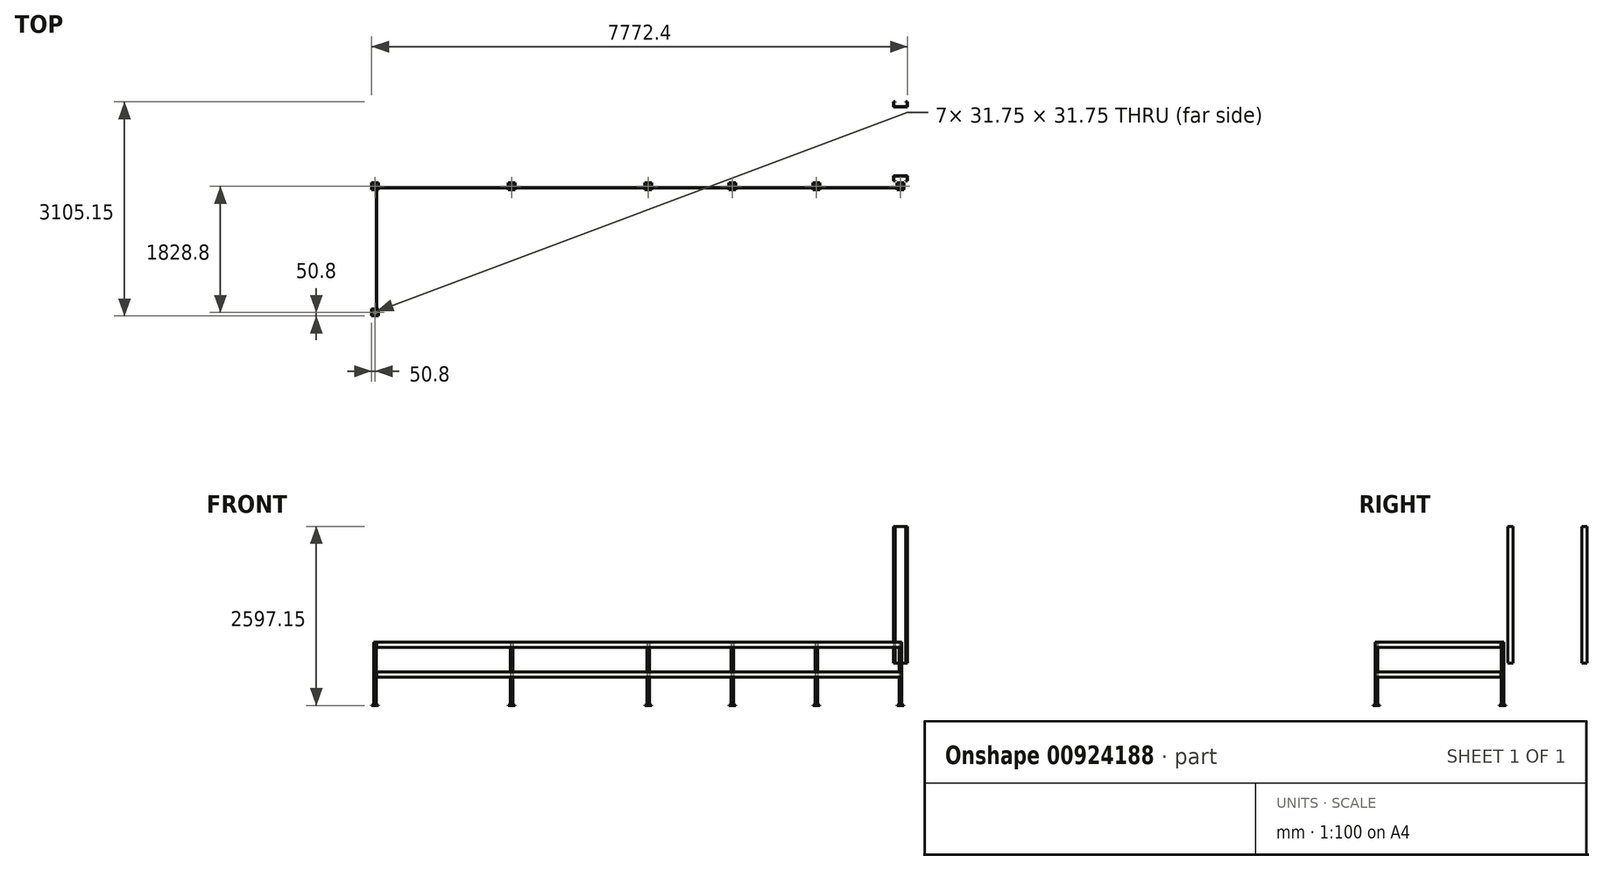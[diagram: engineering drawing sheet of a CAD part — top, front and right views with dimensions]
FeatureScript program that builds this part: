
annotation { "Feature Type Name" : "Feature", "Feature Type Description" : "" }
export const myFeature = defineFeature(function(context is Context, id is Id, definition is map)
    precondition{}
    {
        {
            var Q0;
            Q0=qCreatedBy(makeId("Top.planeOp"),FACE);
            var sketch = newSketch(context, id + "F0", { "sketchPlane" : qUnion([Q0])});
            skLineSegment(sketch, "E0", {"start": v(0, 0) * mm, "end": v(-7620, 0) * mm, "construction": true});
            skLineSegment(sketch, "E1", {"start": v(-7620, 0) * mm, "end": v(-7620, -1828.8) * mm, "construction": true});
            skLineSegment(sketch, "E2", {"start": v(-76.2, 76.2) * mm, "end": v(-101.6, 76.2) * mm});
            skLineSegment(sketch, "E3", {"start": v(-101.6, 76.2) * mm, "end": v(-101.6, 152.4) * mm});
            skLineSegment(sketch, "E4", {"start": v(-101.6, 152.4) * mm, "end": v(101.6, 152.4) * mm});
            skLineSegment(sketch, "E5", {"start": v(101.6, 152.4) * mm, "end": v(101.6, 76.2) * mm});
            skLineSegment(sketch, "E6", {"start": v(101.6, 76.2) * mm, "end": v(76.2, 76.2) * mm});
            skLineSegment(sketch, "E7", {"start": v(-76.2, 76.2) * mm, "end": v(-76.2, 82.55) * mm});
            skLineSegment(sketch, "E8", {"start": v(-76.2, 82.55) * mm, "end": v(-95.25, 82.55) * mm});
            skLineSegment(sketch, "E9", {"start": v(-95.25, 82.55) * mm, "end": v(-95.25, 146.05) * mm});
            skLineSegment(sketch, "E10", {"start": v(-95.25, 146.05) * mm, "end": v(95.25, 146.05) * mm});
            skLineSegment(sketch, "E11", {"start": v(95.25, 146.05) * mm, "end": v(95.25, 82.55) * mm});
            skLineSegment(sketch, "E12", {"start": v(95.25, 82.55) * mm, "end": v(76.2, 82.55) * mm});
            skLineSegment(sketch, "E13", {"start": v(76.2, 82.55) * mm, "end": v(76.2, 76.2) * mm});
            skLineSegment(sketch, "E14", {"start": v(-233.49, 650.88) * mm, "end": v(236.2, 650.88) * mm, "construction": true});
            skLineSegment(sketch, "E15.MirrorCS", {"start": v(76.2, 1219.2) * mm, "end": v(76.2, 1225.55) * mm});
            skLineSegment(sketch, "E16.MirrorCS", {"start": v(-76.2, 1225.55) * mm, "end": v(-76.2, 1219.2) * mm});
            skLineSegment(sketch, "E17.MirrorCS", {"start": v(-76.2, 1225.55) * mm, "end": v(-101.6, 1225.55) * mm});
            skLineSegment(sketch, "E18.MirrorCS", {"start": v(-76.2, 1219.2) * mm, "end": v(-95.25, 1219.2) * mm});
            skLineSegment(sketch, "E19.MirrorCS", {"start": v(95.25, 1219.2) * mm, "end": v(76.2, 1219.2) * mm});
            skLineSegment(sketch, "E20.MirrorCS", {"start": v(101.6, 1225.55) * mm, "end": v(76.2, 1225.55) * mm});
            skLineSegment(sketch, "E21.MirrorCS", {"start": v(-101.6, 1149.35) * mm, "end": v(101.6, 1149.35) * mm});
            skLineSegment(sketch, "E22.MirrorCS", {"start": v(101.6, 1149.35) * mm, "end": v(101.6, 1225.55) * mm});
            skLineSegment(sketch, "E23.MirrorCS", {"start": v(-95.25, 1219.2) * mm, "end": v(-95.25, 1155.7) * mm});
            skLineSegment(sketch, "E24.MirrorCS", {"start": v(-101.6, 1225.55) * mm, "end": v(-101.6, 1149.35) * mm});
            skLineSegment(sketch, "E25.MirrorCS", {"start": v(-95.25, 1155.7) * mm, "end": v(95.25, 1155.7) * mm});
            skLineSegment(sketch, "E26.MirrorCS", {"start": v(95.25, 1155.7) * mm, "end": v(95.25, 1219.2) * mm});
            skLineSegment(sketch, "E27", {"start": v(-609.6, 108.02) * mm, "end": v(-609.6, -185.33) * mm, "construction": true});
            skLineSegment(sketch, "E28", {"start": v(-1828.8, 108.44) * mm, "end": v(-1828.8, -180.27) * mm, "construction": true});
            skLineSegment(sketch, "E29", {"start": v(-3048, 105.92) * mm, "end": v(-3048, -182.8) * mm, "construction": true});
            skLineSegment(sketch, "E30", {"start": v(-4648.2, 106.34) * mm, "end": v(-4648.2, -182.37) * mm, "construction": true});
            skLineSegment(sketch, "E31", {"start": v(-6629.4, 145.72) * mm, "end": v(-6629.4, -360.05) * mm, "construction": true});
            skLineSegment(sketch, "E32", {"start": v(-7914.29, -914.4) * mm, "end": v(-7272.72, -914.4) * mm, "construction": true});
            skLineSegment(sketch, "E33.bottom", {"start": v(19.05, 19.05) * mm, "end": v(-19.05, 19.05) * mm});
            skLineSegment(sketch, "E33.top", {"start": v(19.05, -19.05) * mm, "end": v(-19.05, -19.05) * mm});
            skLineSegment(sketch, "E33.left", {"start": v(19.05, 19.05) * mm, "end": v(19.05, -19.05) * mm});
            skLineSegment(sketch, "E33.right", {"start": v(-19.05, 19.05) * mm, "end": v(-19.05, -19.05) * mm});
            skPoint(sketch, "E33.middle", {"position": v(0, 0) * mm});
            skLineSegment(sketch, "E34.bottom", {"start": v(15.88, 15.87) * mm, "end": v(-15.88, 15.88) * mm});
            skLineSegment(sketch, "E34.top", {"start": v(15.88, -15.88) * mm, "end": v(-15.88, -15.87) * mm});
            skLineSegment(sketch, "E34.left", {"start": v(15.88, 15.87) * mm, "end": v(15.88, -15.87) * mm});
            skLineSegment(sketch, "E34.right", {"start": v(-15.88, 15.87) * mm, "end": v(-15.88, -15.87) * mm});
            skPoint(sketch, "E35.MirrorP", {"position": v(-1219.2, 0) * mm});
            skLineSegment(sketch, "E36.MirrorCS", {"start": v(-1238.25, 19.05) * mm, "end": v(-1238.25, -19.05) * mm});
            skLineSegment(sketch, "E37.MirrorCS", {"start": v(-1235.08, 15.87) * mm, "end": v(-1203.33, 15.87) * mm});
            skLineSegment(sketch, "E38.MirrorCS", {"start": v(-1238.25, -19.05) * mm, "end": v(-1200.15, -19.05) * mm});
            skLineSegment(sketch, "E39.MirrorCS", {"start": v(-1235.08, 15.87) * mm, "end": v(-1235.08, -15.88) * mm});
            skLineSegment(sketch, "E40.MirrorCS", {"start": v(-1203.33, 15.87) * mm, "end": v(-1203.33, -15.88) * mm});
            skLineSegment(sketch, "E41.MirrorCS", {"start": v(-1235.08, -15.88) * mm, "end": v(-1203.33, -15.88) * mm});
            skLineSegment(sketch, "E42.MirrorCS", {"start": v(-1200.15, 19.05) * mm, "end": v(-1200.15, -19.05) * mm});
            skLineSegment(sketch, "E43.MirrorCS", {"start": v(-1238.25, 19.05) * mm, "end": v(-1200.15, 19.05) * mm});
            skPoint(sketch, "E44.MirrorP", {"position": v(-2438.4, 0) * mm});
            skLineSegment(sketch, "E45.MirrorCS", {"start": v(-2419.35, 19.05) * mm, "end": v(-2457.45, 19.05) * mm});
            skLineSegment(sketch, "E46.MirrorCS", {"start": v(-2454.28, 15.87) * mm, "end": v(-2454.28, -15.88) * mm});
            skLineSegment(sketch, "E47.MirrorCS", {"start": v(-2422.53, 15.87) * mm, "end": v(-2422.53, -15.88) * mm});
            skLineSegment(sketch, "E48.MirrorCS", {"start": v(-2419.35, 19.05) * mm, "end": v(-2419.35, -19.05) * mm});
            skLineSegment(sketch, "E49.MirrorCS", {"start": v(-2422.53, 15.87) * mm, "end": v(-2454.28, 15.87) * mm});
            skLineSegment(sketch, "E50.MirrorCS", {"start": v(-2457.45, 19.05) * mm, "end": v(-2457.45, -19.05) * mm});
            skLineSegment(sketch, "E51.MirrorCS", {"start": v(-2419.35, -19.05) * mm, "end": v(-2457.45, -19.05) * mm});
            skLineSegment(sketch, "E52.MirrorCS", {"start": v(-2422.53, -15.88) * mm, "end": v(-2454.28, -15.88) * mm});
            skPoint(sketch, "E53.MirrorP", {"position": v(-3657.6, 0) * mm});
            skLineSegment(sketch, "E54.MirrorCS", {"start": v(-3638.55, 19.05) * mm, "end": v(-3638.55, -19.05) * mm});
            skLineSegment(sketch, "E55.MirrorCS", {"start": v(-3676.65, 19.05) * mm, "end": v(-3638.55, 19.05) * mm});
            skLineSegment(sketch, "E56.MirrorCS", {"start": v(-3673.48, 15.87) * mm, "end": v(-3641.72, 15.87) * mm});
            skLineSegment(sketch, "E57.MirrorCS", {"start": v(-3673.48, -15.88) * mm, "end": v(-3641.72, -15.88) * mm});
            skLineSegment(sketch, "E58.MirrorCS", {"start": v(-3676.65, 19.05) * mm, "end": v(-3676.65, -19.05) * mm});
            skLineSegment(sketch, "E59.MirrorCS", {"start": v(-3641.73, 15.87) * mm, "end": v(-3641.73, -15.88) * mm});
            skLineSegment(sketch, "E60.MirrorCS", {"start": v(-3673.48, 15.87) * mm, "end": v(-3673.48, -15.88) * mm});
            skLineSegment(sketch, "E61.MirrorCS", {"start": v(-3676.65, -19.05) * mm, "end": v(-3638.55, -19.05) * mm});
            skPoint(sketch, "E62.MirrorP", {"position": v(-5638.8, 0) * mm});
            skLineSegment(sketch, "E63.MirrorCS", {"start": v(-5619.75, -19.05) * mm, "end": v(-5657.85, -19.05) * mm});
            skLineSegment(sketch, "E64.MirrorCS", {"start": v(-5622.92, -15.88) * mm, "end": v(-5654.68, -15.88) * mm});
            skLineSegment(sketch, "E65.MirrorCS", {"start": v(-5619.75, 19.05) * mm, "end": v(-5619.75, -19.05) * mm});
            skLineSegment(sketch, "E66.MirrorCS", {"start": v(-5619.75, 19.05) * mm, "end": v(-5657.85, 19.05) * mm});
            skLineSegment(sketch, "E67.MirrorCS", {"start": v(-5654.67, 15.87) * mm, "end": v(-5654.67, -15.88) * mm});
            skLineSegment(sketch, "E68.MirrorCS", {"start": v(-5657.85, 19.05) * mm, "end": v(-5657.85, -19.05) * mm});
            skLineSegment(sketch, "E69.MirrorCS", {"start": v(-5622.92, 15.87) * mm, "end": v(-5654.68, 15.87) * mm});
            skLineSegment(sketch, "E70.MirrorCS", {"start": v(-5622.92, 15.87) * mm, "end": v(-5622.92, -15.88) * mm});
            skPoint(sketch, "E71.MirrorP", {"position": v(-7620, 0) * mm});
            skLineSegment(sketch, "E72.MirrorCS", {"start": v(-7639.05, -19.05) * mm, "end": v(-7600.95, -19.05) * mm});
            skLineSegment(sketch, "E73.MirrorCS", {"start": v(-7639.05, 19.05) * mm, "end": v(-7600.95, 19.05) * mm});
            skLineSegment(sketch, "E74.MirrorCS", {"start": v(-7600.95, 19.05) * mm, "end": v(-7600.95, -19.05) * mm});
            skLineSegment(sketch, "E75.MirrorCS", {"start": v(-7635.88, 15.87) * mm, "end": v(-7604.13, 15.87) * mm});
            skLineSegment(sketch, "E76.MirrorCS", {"start": v(-7635.88, 15.87) * mm, "end": v(-7635.88, -15.88) * mm});
            skLineSegment(sketch, "E77.MirrorCS", {"start": v(-7639.05, 19.05) * mm, "end": v(-7639.05, -19.05) * mm});
            skLineSegment(sketch, "E78.MirrorCS", {"start": v(-7635.88, -15.88) * mm, "end": v(-7604.13, -15.88) * mm});
            skLineSegment(sketch, "E79.MirrorCS", {"start": v(-7604.13, 15.87) * mm, "end": v(-7604.13, -15.88) * mm});
            skPoint(sketch, "E80.MirrorP", {"position": v(-7620, -1828.8) * mm});
            skLineSegment(sketch, "E81.MirrorCS", {"start": v(-7639.05, -1809.75) * mm, "end": v(-7600.95, -1809.75) * mm});
            skLineSegment(sketch, "E82.MirrorCS", {"start": v(-7635.88, -1844.67) * mm, "end": v(-7604.12, -1844.67) * mm});
            skLineSegment(sketch, "E83.MirrorCS", {"start": v(-7604.13, -1844.67) * mm, "end": v(-7604.13, -1812.92) * mm});
            skLineSegment(sketch, "E84.MirrorCS", {"start": v(-7639.05, -1847.85) * mm, "end": v(-7639.05, -1809.75) * mm});
            skLineSegment(sketch, "E85.MirrorCS", {"start": v(-7600.95, -1847.85) * mm, "end": v(-7600.95, -1809.75) * mm});
            skLineSegment(sketch, "E86.MirrorCS", {"start": v(-7639.05, -1847.85) * mm, "end": v(-7600.95, -1847.85) * mm});
            skLineSegment(sketch, "E87.MirrorCS", {"start": v(-7635.88, -1812.92) * mm, "end": v(-7604.12, -1812.92) * mm});
            skLineSegment(sketch, "E88.MirrorCS", {"start": v(-7635.88, -1844.67) * mm, "end": v(-7635.88, -1812.92) * mm});
            skSolve(sketch);
        }
        {
            var Q0;
            Q0=qCreatedBy(makeId("Top.planeOp"),FACE);
            cPlane(context, id + "F1", {"entities" : qUnion([Q0]), "cplaneType" : CPlaneType.OFFSET, "offset" : 609.6 * mm, "width" : 152.4 * mm, "height" : 152.4 * mm});
        }
        {
            var Q0;
            Q0=qCreatedBy(id+"F1.planeOp",FACE);
            var sketch = newSketch(context, id + "F2", { "sketchPlane" : qUnion([Q0])});
            skLineSegment(sketch, "E89", {"start": v(-76.2, 82.55) * mm, "end": v(-76.2, 76.2) * mm});
            skLineSegment(sketch, "E90", {"start": v(-76.2, 76.2) * mm, "end": v(-101.6, 76.2) * mm});
            skLineSegment(sketch, "E91", {"start": v(-101.6, 76.2) * mm, "end": v(-101.6, 152.4) * mm});
            skLineSegment(sketch, "E92", {"start": v(-101.6, 152.4) * mm, "end": v(101.6, 152.4) * mm});
            skLineSegment(sketch, "E93", {"start": v(101.6, 152.4) * mm, "end": v(101.6, 76.2) * mm});
            skLineSegment(sketch, "E94", {"start": v(101.6, 76.2) * mm, "end": v(76.2, 76.2) * mm});
            skLineSegment(sketch, "E95", {"start": v(76.2, 76.2) * mm, "end": v(76.2, 82.55) * mm});
            skLineSegment(sketch, "E96", {"start": v(76.2, 82.55) * mm, "end": v(95.25, 82.55) * mm});
            skLineSegment(sketch, "E97", {"start": v(95.25, 82.55) * mm, "end": v(95.25, 146.05) * mm});
            skLineSegment(sketch, "E98", {"start": v(95.25, 146.05) * mm, "end": v(-95.25, 146.05) * mm});
            skLineSegment(sketch, "E99", {"start": v(-95.25, 146.05) * mm, "end": v(-95.25, 82.55) * mm});
            skLineSegment(sketch, "E100", {"start": v(-95.25, 82.55) * mm, "end": v(-76.2, 82.55) * mm});
            skLineSegment(sketch, "E101.MirrorCS", {"start": v(101.6, 1225.55) * mm, "end": v(76.2, 1225.55) * mm});
            skLineSegment(sketch, "E102.MirrorCS", {"start": v(-76.2, 1219.2) * mm, "end": v(-76.2, 1225.55) * mm});
            skLineSegment(sketch, "E103.MirrorCS", {"start": v(76.2, 1225.55) * mm, "end": v(76.2, 1219.2) * mm});
            skLineSegment(sketch, "E104.MirrorCS", {"start": v(-95.25, 1219.2) * mm, "end": v(-76.2, 1219.2) * mm});
            skLineSegment(sketch, "E105.MirrorCS", {"start": v(76.2, 1219.2) * mm, "end": v(95.25, 1219.2) * mm});
            skLineSegment(sketch, "E106.MirrorCS", {"start": v(-76.2, 1225.55) * mm, "end": v(-101.6, 1225.55) * mm});
            skLineSegment(sketch, "E107.MirrorCS", {"start": v(101.6, 1149.35) * mm, "end": v(101.6, 1225.55) * mm});
            skLineSegment(sketch, "E108.MirrorCS", {"start": v(95.25, 1155.7) * mm, "end": v(-95.25, 1155.7) * mm});
            skLineSegment(sketch, "E109.MirrorCS", {"start": v(95.25, 1219.2) * mm, "end": v(95.25, 1155.7) * mm});
            skLineSegment(sketch, "E110.MirrorCS", {"start": v(-95.25, 1155.7) * mm, "end": v(-95.25, 1219.2) * mm});
            skLineSegment(sketch, "E111.MirrorCS", {"start": v(-101.6, 1225.55) * mm, "end": v(-101.6, 1149.35) * mm});
            skLineSegment(sketch, "E112.MirrorCS", {"start": v(-101.6, 1149.35) * mm, "end": v(101.6, 1149.35) * mm});
            skSolve(sketch);
        }
        {
            var Q0;
            Q0 = qSketchRegion(id + "F2", true);
            extrude(context, id + "F3", {"entities" : qUnion([Q0]), "depth" : 1981.2 * mm, "offsetDistance" : 25.4 * mm});
        }
        {
            var Q0;
            Q0=makeQuery(id+"F0.imprint","IMPRINT",FACE,{"disambiguationData":[TD([[makeQuery(id+"F0.imprint","IMPRINT",EDGE,{"derivedFrom":sQuery(id+"F0.wireOp",EDGE,"E81.MirrorCS")}),-1.0]])]});
            var Q1;
            Q1=makeQuery(id+"F0.imprint","IMPRINT",FACE,{"disambiguationData":[TD([[makeQuery(id+"F0.imprint","IMPRINT",EDGE,{"derivedFrom":sQuery(id+"F0.wireOp",EDGE,"E72.MirrorCS")}),1.0]])]});
            var Q2;
            Q2=makeQuery(id+"F0.imprint","IMPRINT",FACE,{"disambiguationData":[TD([[makeQuery(id+"F0.imprint","IMPRINT",EDGE,{"derivedFrom":sQuery(id+"F0.wireOp",EDGE,"E63.MirrorCS")}),-1.0]])]});
            var Q3;
            Q3=makeQuery(id+"F0.imprint","IMPRINT",FACE,{"disambiguationData":[TD([[makeQuery(id+"F0.imprint","IMPRINT",EDGE,{"derivedFrom":sQuery(id+"F0.wireOp",EDGE,"E54.MirrorCS")}),-1.0]])]});
            var Q4;
            Q4=makeQuery(id+"F0.imprint","IMPRINT",FACE,{"disambiguationData":[TD([[makeQuery(id+"F0.imprint","IMPRINT",EDGE,{"derivedFrom":sQuery(id+"F0.wireOp",EDGE,"E45.MirrorCS")}),1.0]])]});
            var Q5;
            Q5=makeQuery(id+"F0.imprint","IMPRINT",FACE,{"disambiguationData":[TD([[makeQuery(id+"F0.imprint","IMPRINT",EDGE,{"derivedFrom":sQuery(id+"F0.wireOp",EDGE,"E36.MirrorCS")}),1.0]])]});
            var Q6;
            Q6=makeQuery(id+"F0.imprint","IMPRINT",FACE,{"disambiguationData":[TD([[makeQuery(id+"F0.imprint","IMPRINT",EDGE,{"derivedFrom":sQuery(id+"F0.wireOp",EDGE,"E33.bottom")}),1.0]])]});
            extrude(context, id + "F4", {"entities" : qUnion([Q0, Q1, Q2, Q3, Q4, Q5, Q6]), "depth" : 3 * 304.8 * mm, "offsetDistance" : 25.4 * mm});
        }
        {
            var Q0;
            Q0=qCreatedBy(makeId("Top.planeOp"),FACE);
            var sketch = newSketch(context, id + "F5", { "sketchPlane" : qUnion([Q0])});
            skLineSegment(sketch, "E113.bottom", {"start": v(50.8, 50.8) * mm, "end": v(-50.8, 50.8) * mm});
            skLineSegment(sketch, "E113.top", {"start": v(50.8, -50.8) * mm, "end": v(-50.8, -50.8) * mm});
            skLineSegment(sketch, "E113.left", {"start": v(50.8, 50.8) * mm, "end": v(50.8, -50.8) * mm});
            skLineSegment(sketch, "E113.right", {"start": v(-50.8, 50.8) * mm, "end": v(-50.8, -50.8) * mm});
            skPoint(sketch, "E113.middle", {"position": v(0, 0) * mm});
            skLineSegment(sketch, "E114.MirrorCS", {"start": v(-1168.4, 50.8) * mm, "end": v(-1168.4, -50.8) * mm});
            skLineSegment(sketch, "E115.MirrorCS", {"start": v(-1270, -50.8) * mm, "end": v(-1168.4, -50.8) * mm});
            skLineSegment(sketch, "E116.MirrorCS", {"start": v(-1270, 50.8) * mm, "end": v(-1270, -50.8) * mm});
            skPoint(sketch, "E117.MirrorP", {"position": v(-1219.2, 0) * mm});
            skLineSegment(sketch, "E118.MirrorCS", {"start": v(-1270, 50.8) * mm, "end": v(-1168.4, 50.8) * mm});
            skLineSegment(sketch, "E119.MirrorCS", {"start": v(-2387.6, 50.8) * mm, "end": v(-2387.6, -50.8) * mm});
            skPoint(sketch, "E120.MirrorP", {"position": v(-2438.4, 0) * mm});
            skLineSegment(sketch, "E121.MirrorCS", {"start": v(-2387.6, -50.8) * mm, "end": v(-2489.2, -50.8) * mm});
            skLineSegment(sketch, "E122.MirrorCS", {"start": v(-2489.2, 50.8) * mm, "end": v(-2489.2, -50.8) * mm});
            skLineSegment(sketch, "E123.MirrorCS", {"start": v(-2387.6, 50.8) * mm, "end": v(-2489.2, 50.8) * mm});
            skPoint(sketch, "E124.MirrorP", {"position": v(-3657.6, 0) * mm});
            skLineSegment(sketch, "E125.MirrorCS", {"start": v(-3708.4, 50.8) * mm, "end": v(-3606.8, 50.8) * mm});
            skLineSegment(sketch, "E126.MirrorCS", {"start": v(-3606.8, 50.8) * mm, "end": v(-3606.8, -50.8) * mm});
            skLineSegment(sketch, "E127.MirrorCS", {"start": v(-3708.4, -50.8) * mm, "end": v(-3606.8, -50.8) * mm});
            skLineSegment(sketch, "E128.MirrorCS", {"start": v(-3708.4, 50.8) * mm, "end": v(-3708.4, -50.8) * mm});
            skLineSegment(sketch, "E129.MirrorCS", {"start": v(-5588, 50.8) * mm, "end": v(-5689.6, 50.8) * mm});
            skLineSegment(sketch, "E130.MirrorCS", {"start": v(-5689.6, 50.8) * mm, "end": v(-5689.6, -50.8) * mm});
            skLineSegment(sketch, "E131.MirrorCS", {"start": v(-5588, -50.8) * mm, "end": v(-5689.6, -50.8) * mm});
            skLineSegment(sketch, "E132.MirrorCS", {"start": v(-5588, 50.8) * mm, "end": v(-5588, -50.8) * mm});
            skLineSegment(sketch, "E133.MirrorCS", {"start": v(-7569.2, 50.8) * mm, "end": v(-7569.2, -50.8) * mm});
            skLineSegment(sketch, "E134.MirrorCS", {"start": v(-7670.8, -50.8) * mm, "end": v(-7569.2, -50.8) * mm});
            skLineSegment(sketch, "E135.MirrorCS", {"start": v(-7670.8, 50.8) * mm, "end": v(-7670.8, -50.8) * mm});
            skLineSegment(sketch, "E136.MirrorCS", {"start": v(-7670.8, 50.8) * mm, "end": v(-7569.2, 50.8) * mm});
            skLineSegment(sketch, "E137.MirrorCS", {"start": v(-7569.2, -1879.6) * mm, "end": v(-7569.2, -1778) * mm});
            skLineSegment(sketch, "E138.MirrorCS", {"start": v(-7670.8, -1778) * mm, "end": v(-7569.2, -1778) * mm});
            skLineSegment(sketch, "E139.MirrorCS", {"start": v(-7670.8, -1879.6) * mm, "end": v(-7569.2, -1879.6) * mm});
            skLineSegment(sketch, "E140.MirrorCS", {"start": v(-7670.8, -1879.6) * mm, "end": v(-7670.8, -1778) * mm});
            skSolve(sketch);
        }
        {
            var Q0;
            Q0 = qSketchRegion(id + "F5", true);
            extrude(context, id + "F6", {"entities" : qUnion([Q0]), "oppositeDirection" : true, "depth" : 6.35 * mm, "offsetDistance" : 25.4 * mm});
        }
        {
            var Q0;
            Q0=qCreatedBy(makeId("Front.planeOp"),FACE);
            cPlane(context, id + "F7", {"entities" : qUnion([Q0]), "cplaneType" : CPlaneType.OFFSET, "offset" : 19.05 * mm, "width" : 152.4 * mm, "height" : 152.4 * mm});
        }
        {
            var Q0;
            Q0=qCreatedBy(id+"F7.planeOp",FACE);
            var sketch = newSketch(context, id + "F8", { "sketchPlane" : qUnion([Q0])});
            skLineSegment(sketch, "E141", {"start": v(19.05, 914.4) * mm, "end": v(-7639.05, 914.4) * mm});
            skLineSegment(sketch, "E142", {"start": v(-7639.05, 914.4) * mm, "end": v(-7639.05, 838.2) * mm});
            skLineSegment(sketch, "E143", {"start": v(-7639.05, 838.2) * mm, "end": v(19.05, 838.2) * mm});
            skLineSegment(sketch, "E144", {"start": v(19.05, 838.2) * mm, "end": v(19.05, 914.4) * mm});
            skLineSegment(sketch, "E145", {"start": v(-8057.64, 660.4) * mm, "end": v(414.74, 660.4) * mm, "construction": true});
            skLineSegment(sketch, "E146.MirrorCS", {"start": v(19.05, 482.6) * mm, "end": v(19.05, 406.4) * mm});
            skLineSegment(sketch, "E147.MirrorCS", {"start": v(-7639.05, 406.4) * mm, "end": v(-7639.05, 482.6) * mm});
            skLineSegment(sketch, "E148.MirrorCS", {"start": v(-7639.05, 482.6) * mm, "end": v(19.05, 482.6) * mm});
            skLineSegment(sketch, "E149.MirrorCS", {"start": v(19.05, 406.4) * mm, "end": v(-7639.05, 406.4) * mm});
            skSolve(sketch);
        }
        {
            var Q0;
            Q0 = qSketchRegion(id + "F8", true);
            extrude(context, id + "F9", {"entities" : qUnion([Q0]), "depth" : 6.35 * mm, "offsetDistance" : 25.4 * mm});
        }
        {
            var Q0;
            Q0=qCreatedBy(makeId("Right.planeOp"),FACE);
            cPlane(context, id + "F10", {"entities" : qUnion([Q0]), "cplaneType" : CPlaneType.OFFSET, "offset" : 7600.95 * mm, "oppositeDirection" : true, "width" : 152.4 * mm, "height" : 152.4 * mm});
        }
        {
            var Q0;
            Q0=qCreatedBy(id+"F10.planeOp",FACE);
            var sketch = newSketch(context, id + "F11", { "sketchPlane" : qUnion([Q0])});
            skLineSegment(sketch, "E150", {"start": v(-25.4, 914.4) * mm, "end": v(-25.4, 838.2) * mm});
            skLineSegment(sketch, "E151", {"start": v(-25.4, 838.2) * mm, "end": v(-1847.85, 838.2) * mm});
            skLineSegment(sketch, "E152", {"start": v(-1847.85, 838.2) * mm, "end": v(-1847.85, 914.4) * mm});
            skLineSegment(sketch, "E153", {"start": v(-1847.85, 914.4) * mm, "end": v(-25.4, 914.4) * mm});
            skLineSegment(sketch, "E154", {"start": v(-1613.68, 660.4) * mm, "end": v(-2082.05, 660.4) * mm, "construction": true});
            skLineSegment(sketch, "E155.MirrorCS", {"start": v(-25.4, 482.6) * mm, "end": v(-1847.85, 482.6) * mm});
            skLineSegment(sketch, "E156.MirrorCS", {"start": v(-1847.85, 406.4) * mm, "end": v(-25.4, 406.4) * mm});
            skLineSegment(sketch, "E157.MirrorCS", {"start": v(-1847.85, 482.6) * mm, "end": v(-1847.85, 406.4) * mm});
            skLineSegment(sketch, "E158.MirrorCS", {"start": v(-25.4, 406.4) * mm, "end": v(-25.4, 482.6) * mm});
            skSolve(sketch);
        }
        {
            var Q0;
            Q0 = qSketchRegion(id + "F11", true);
            extrude(context, id + "F12", {"entities" : qUnion([Q0]), "depth" : 6.35 * mm, "offsetDistance" : 25.4 * mm});
        }
    });
